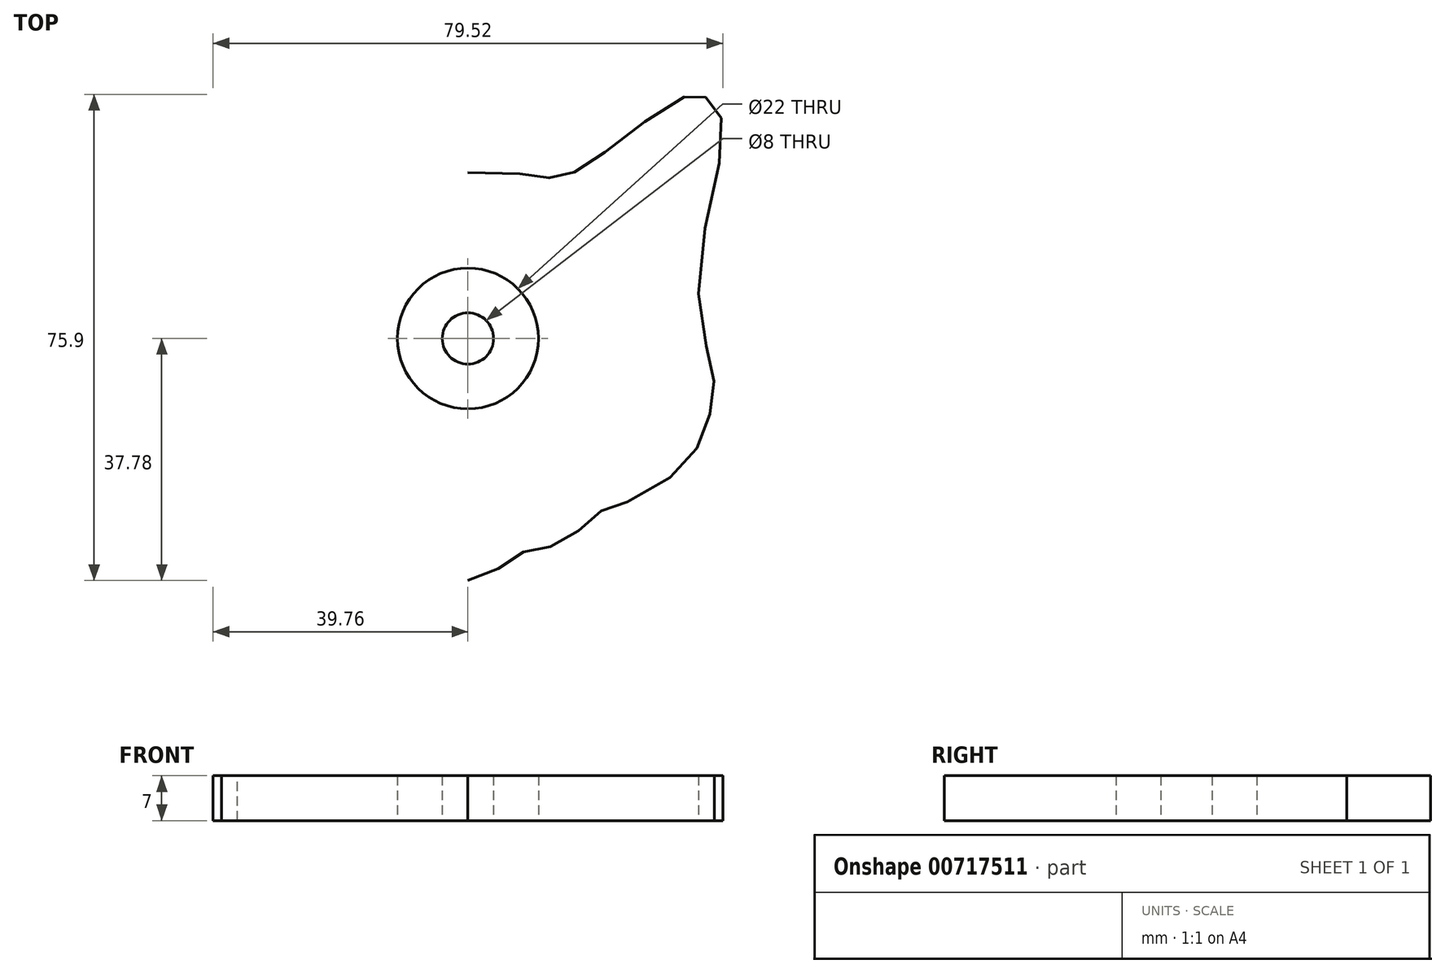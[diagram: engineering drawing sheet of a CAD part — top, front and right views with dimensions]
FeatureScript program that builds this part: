
annotation { "Feature Type Name" : "Feature", "Feature Type Description" : "" }
export const myFeature = defineFeature(function(context is Context, id is Id, definition is map)
    precondition{}
    {
        {
            assignVariable(context, id + "F0", {"name" : "thickness", "anyValue" : 7 * mm});
        }
        {
            var Q0;
            Q0=qCreatedBy(makeId("Top.planeOp"),FACE);
            var sketch = newSketch(context, id + "F1", { "sketchPlane" : qUnion([Q0])});
            skCircle(sketch, "E0", {"center": v(0, 0) * mm, "radius": 11 * mm});
            skCircle(sketch, "E1", {"center": v(0, 0) * mm, "radius": 4 * mm});
            skSolve(sketch);
        }
        {
            var Q0;
            Q0=makeQuery(id+"F1.imprint","IMPRINT",FACE,{"disambiguationData":[TD([[makeQuery(id+"F1.imprint","IMPRINT",EDGE,{"derivedFrom":sQuery(id+"F1.wireOp",EDGE,"E0")}),1.0]])]});
            extrude(context, id + "F2", {"entities" : qUnion([Q0]), "depth" : getVariable(context, 'thickness'), "offsetDistance" : 25.4 * mm});
        }
        {
            var Q0;
            Q0=qCreatedBy(makeId("Top.planeOp"),FACE);
            var sketch = newSketch(context, id + "F3", { "sketchPlane" : qUnion([Q0])});
            skCircle(sketch, "E2", {"center": v(0, 0) * mm, "radius": 76.2 * mm, "construction": true});
            skCircle(sketch, "E3", {"center": v(0, 0) * mm, "radius": 11 * mm});
            skLineSegment(sketch, "E4.bottom", {"start": v(50.8, -50.8) * mm, "end": v(-50.8, -50.8) * mm, "construction": true});
            skLineSegment(sketch, "E4.top", {"start": v(50.8, 50.8) * mm, "end": v(-50.8, 50.8) * mm, "construction": true});
            skLineSegment(sketch, "E4.left", {"start": v(50.8, -50.8) * mm, "end": v(50.8, 50.8) * mm, "construction": true});
            skLineSegment(sketch, "E4.right", {"start": v(-50.8, -50.8) * mm, "end": v(-50.8, 50.8) * mm, "construction": true});
            skFitSpline(sketch, "E5", {"points": [v(0, 25.89) * mm, v(-10.97, 25.46) * mm, v(-13.35, 25.03) * mm, v(-17.23, 26.32) * mm, v(-23.92, 31.07) * mm, v(-33.85, 37.76) * mm, v(-36.23, 37.98) * mm, v(-38.6, 36.47) * mm, v(-39.68, 30.64) * mm, v(-36.01, 9.92) * mm, v(-37.74, -3.46) * mm, v(-38.38, -8.64) * mm, v(-36.66, -15.12) * mm, v(-32.77, -20.73) * mm, v(-23.28, -26.13) * mm, v(-20.69, -26.99) * mm, v(-17.02, -30.23) * mm, v(-12.48, -32.6) * mm, v(-8.82, -33.25) * mm, v(-4.93, -35.84) * mm, v(0, -37.78) * mm], "startDerivative": vector(-200.3, -0.89) * mm, "endDerivative": vector(113.08, -33.73) * mm});
            skLineSegment(sketch, "E6", {"start": v(0, 50.8) * mm, "end": v(0, -50.8) * mm, "construction": true});
            skFitSpline(sketch, "E7.MirrorCS", {"points": [v(0, 25.89) * mm, v(10.97, 25.46) * mm, v(13.35, 25.03) * mm, v(17.23, 26.32) * mm, v(23.92, 31.07) * mm, v(33.85, 37.76) * mm, v(36.23, 37.98) * mm, v(38.6, 36.47) * mm, v(39.68, 30.64) * mm, v(36.01, 9.92) * mm, v(37.74, -3.46) * mm, v(38.38, -8.64) * mm, v(36.66, -15.12) * mm, v(32.77, -20.73) * mm, v(23.28, -26.13) * mm, v(20.69, -26.99) * mm, v(17.02, -30.23) * mm, v(12.48, -32.6) * mm, v(8.82, -33.25) * mm, v(4.93, -35.84) * mm, v(0, -37.78) * mm], "startDerivative": vector(200.3, -0.89) * mm, "endDerivative": vector(-113.08, -33.73) * mm});
            skSolve(sketch);
        }
        {
            var Q0;
            Q0=makeQuery(id+"F3.imprint","IMPRINT",FACE,{"disambiguationData":[TD([[makeQuery(id+"F3.imprint","IMPRINT",EDGE,{"derivedFrom":sQuery(id+"F3.wireOp",EDGE,"E3")}),-1.0]])]});
            var Q1;
            Q1=makeQuery(id+"F2.opExtrude","CAP_FACE",FACE,{"disambiguationData":[OSD([sQuery(id+"F1.wireOp",EDGE,"E0"),sQuery(id+"F1.wireOp",EDGE,"E1")])],"isStart":false});
            extrude(context, id + "F4", {"entities" : qUnion([Q0]), "endBound" : BoundingType.UP_TO_SURFACE, "depth" : 25.4 * mm, "endBoundEntityFace" : qUnion([Q1]), "offsetDistance" : 25.4 * mm});
        }
    });
